# Revit family: ELUHAD141455
name_source: partatom
category: Plumbing Fixtures
units: mm (PartAtom-declared; Revit-internal decimal feet)

## family parameters
Always vertical = Yes
Cut with Voids When Loaded = No
OmniClass Number = 23.45.05.14.14.27
OmniClass Title = Service Sinks
Part Type = Normal
Room Calculation Point = No
Round Connector Dimension = Use Radius
Shared = No
Work Plane-Based = No

## types (1)
- ELUHAD141455
    Assembly Code = D2010410
    Bowl 1 Dimensions = 14 inch x 14 inch x 5-3/8 inch
    Bowl Length = 1' - 2"
    Bowl Width = 1' - 2"
    CL Sink to CL Drain = 0' - 0"
    Cutout Template # = 1000001265
    Description = Lustertone Single Bowl Sink
    Drain Location = 0' - 5"
    Drain Locations = Rear Center
    Drain Size = 3-1/2 inch (89mm)
    Finish = Lustrous Satin
    Gauge = 18
    Installation Type = Undermount
    Manufacturer = Elkay Manufacturing
    MasterFormat Number = 22.42.16.16
    MasterFormat Title = Commercial Sinks
    Material = 304 Stainless Steel
    Minimum Cabinet Size = 21 inch
    Model = Lustertone Undermount
    Mounting Hardware = Undermount brackets sold separately
    Nominal Dia = 0' - 1 1/2"
    Nominal Radius = 0' - 0 3/4"
    Number of Bowls = 1
    OmniClass Code = 23.45.05.14.14.27
    OmniClass Title = Service Sinks
    Sanitary Flow Rate = 10 GPM
    Sink Depth = 0' - 5 3/8"
    Sink Dimensions = 16 1/2 inch x 16-1/2 inch x 5-3/8 inch
    Sink Ledge Back Width = 0' - 1 1/4"
    Sink Ledge Corner Width = 0' - 1 1/4"
    Sink Ledge Front Width = 0' - 1 1/4"
    Sink Ledge Sides Width = 0' - 1 1/4"
    Sink Length = 1' - 4 1/2"
    Sink Material = Metal - Steel - Stainless - Chrome
    Sink Width = 1' - 4 1/2"
    Sound Deadening = Bottom only pads
    Template Included = Yes
    URL = www.elkayusa.com

## geometry (parser evidence)
native form markers: Sweep x2
no freeform markers — native parametric forms only
